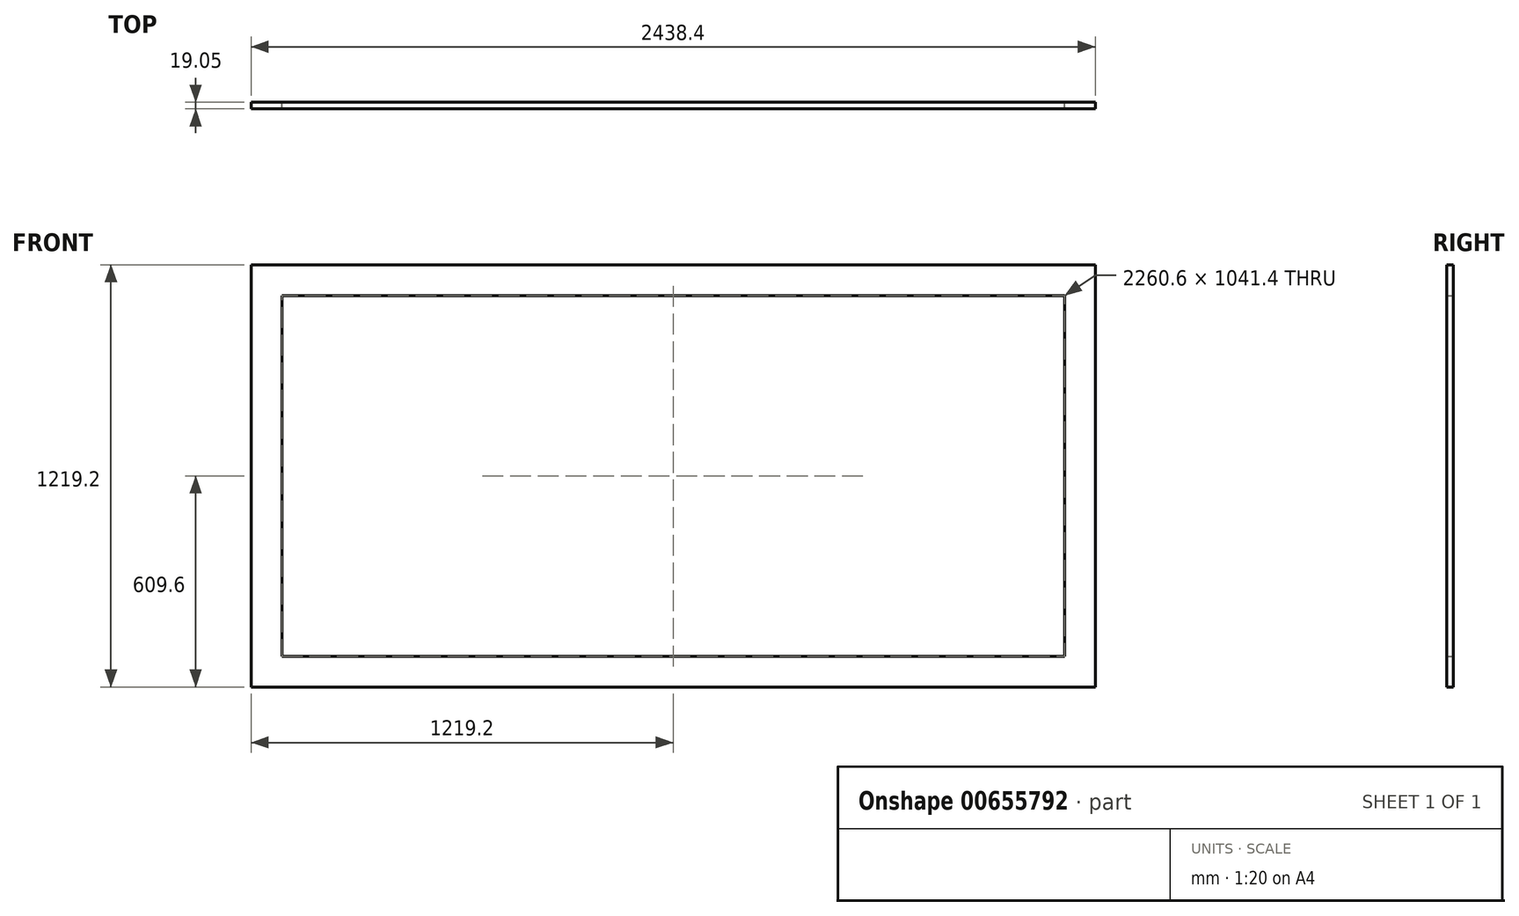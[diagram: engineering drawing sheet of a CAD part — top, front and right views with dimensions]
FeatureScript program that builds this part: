
annotation { "Feature Type Name" : "Feature", "Feature Type Description" : "" }
export const myFeature = defineFeature(function(context is Context, id is Id, definition is map)
    precondition{}
    {
        {
            var Q0;
            Q0=qCreatedBy(makeId("Front.planeOp"),FACE);
            var sketch = newSketch(context, id + "F0", { "sketchPlane" : qUnion([Q0])});
            skLineSegment(sketch, "E0.bottom", {"start": v(1219.2, 609.6) * mm, "end": v(-1219.2, 609.6) * mm});
            skLineSegment(sketch, "E0.top", {"start": v(1219.2, -609.6) * mm, "end": v(-1219.2, -609.6) * mm});
            skLineSegment(sketch, "E0.left", {"start": v(1219.2, 609.6) * mm, "end": v(1219.2, -609.6) * mm});
            skLineSegment(sketch, "E0.right", {"start": v(-1219.2, 609.6) * mm, "end": v(-1219.2, -609.6) * mm});
            skPoint(sketch, "E0.middle", {"position": v(0, 0) * mm});
            skLineSegment(sketch, "E1.bottom", {"start": v(1130.3, -520.7) * mm, "end": v(-1130.3, -520.7) * mm});
            skLineSegment(sketch, "E1.top", {"start": v(1130.3, 520.7) * mm, "end": v(-1130.3, 520.7) * mm});
            skLineSegment(sketch, "E1.left", {"start": v(1130.3, -520.7) * mm, "end": v(1130.3, 520.7) * mm});
            skLineSegment(sketch, "E1.right", {"start": v(-1130.3, -520.7) * mm, "end": v(-1130.3, 520.7) * mm});
            skLineSegment(sketch, "E2", {"start": v(-1219.2, 609.6) * mm, "end": v(-1130.3, 520.7) * mm});
            skLineSegment(sketch, "E3", {"start": v(1130.3, 520.7) * mm, "end": v(1219.2, 609.6) * mm});
            skLineSegment(sketch, "E4", {"start": v(1219.2, -609.6) * mm, "end": v(1130.3, -520.7) * mm});
            skLineSegment(sketch, "E5", {"start": v(-1219.2, -609.6) * mm, "end": v(-1130.3, -520.7) * mm});
            skSolve(sketch);
        }
        {
            var Q0;
            Q0=makeQuery(id+"F0.imprint","IMPRINT",FACE,{"disambiguationData":[TD([[makeQuery(id+"F0.imprint","IMPRINT",EDGE,{"derivedFrom":sQuery(id+"F0.wireOp",EDGE,"E0.bottom")}),1.0]])]});
            var Q1;
            Q1=makeQuery(id+"F0.imprint","IMPRINT",FACE,{"disambiguationData":[TD([[makeQuery(id+"F0.imprint","IMPRINT",EDGE,{"derivedFrom":sQuery(id+"F0.wireOp",EDGE,"E0.left")}),-1.0]])]});
            var Q2;
            Q2=makeQuery(id+"F0.imprint","IMPRINT",FACE,{"disambiguationData":[TD([[makeQuery(id+"F0.imprint","IMPRINT",EDGE,{"derivedFrom":sQuery(id+"F0.wireOp",EDGE,"E0.top")}),-1.0]])]});
            var Q3;
            Q3=makeQuery(id+"F0.imprint","IMPRINT",FACE,{"disambiguationData":[TD([[makeQuery(id+"F0.imprint","IMPRINT",EDGE,{"derivedFrom":sQuery(id+"F0.wireOp",EDGE,"E0.right")}),1.0]])]});
            extrude(context, id + "F1", {"entities" : qUnion([Q0, Q1, Q2, Q3]), "depth" : 19.05 * mm, "offsetDistance" : 25.4 * mm});
        }
    });
